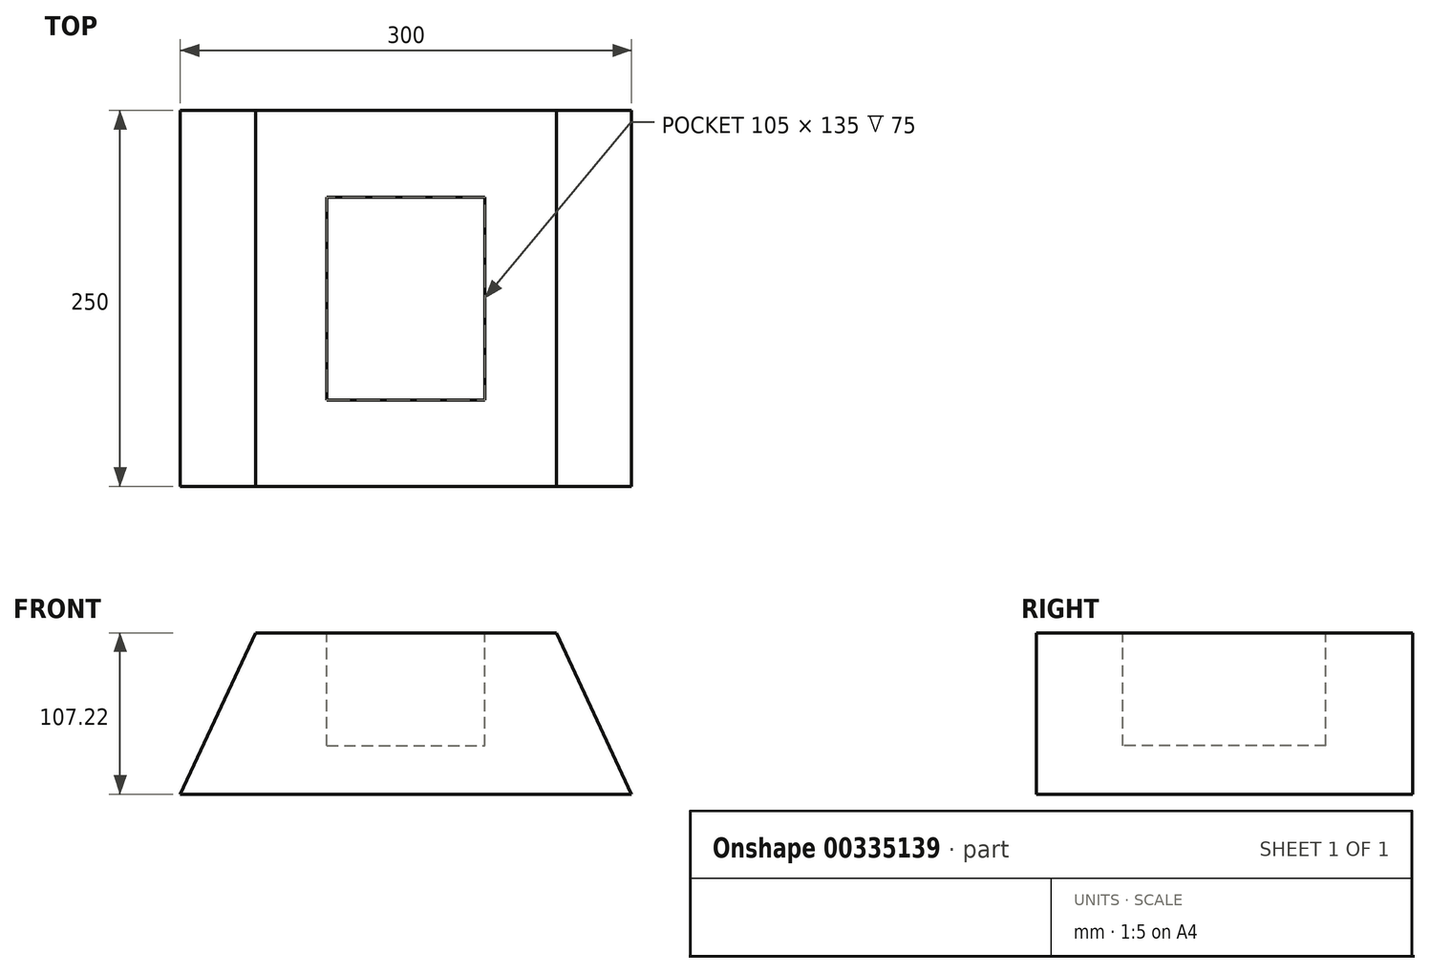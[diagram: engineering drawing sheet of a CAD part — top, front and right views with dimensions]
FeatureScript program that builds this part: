
annotation { "Feature Type Name" : "Feature", "Feature Type Description" : "" }
export const myFeature = defineFeature(function(context is Context, id is Id, definition is map)
    precondition{}
    {
        {
            var Q0;
            Q0=qCreatedBy(makeId("Front.planeOp"),FACE);
            var sketch = newSketch(context, id + "F0", { "sketchPlane" : qUnion([Q0])});
            skLineSegment(sketch, "E0.top", {"start": v(-124.12, -60.52) * mm, "end": v(175.88, -60.52) * mm});
            skLineSegment(sketch, "E1", {"start": v(-124.12, -60.52) * mm, "end": v(-74.12, 46.7) * mm});
            skLineSegment(sketch, "E2", {"start": v(-74.12, 46.7) * mm, "end": v(125.88, 46.7) * mm});
            skLineSegment(sketch, "E3", {"start": v(125.88, 46.7) * mm, "end": v(175.88, -60.52) * mm});
            skSolve(sketch);
        }
        {
            var Q0;
            Q0=makeQuery(id+"F0.imprint","IMPRINT",FACE,{"disambiguationData":[TD([[makeQuery(id+"F0.imprint","IMPRINT",EDGE,{"derivedFrom":sQuery(id+"F0.wireOp",EDGE,"E0.bottom")}),-1.0]])]});
            var Q1;
            Q1=makeQuery(id+"F0.imprint","IMPRINT",FACE,{"disambiguationData":[TD([[makeQuery(id+"F0.imprint","IMPRINT",EDGE,{"derivedFrom":sQuery(id+"F0.wireOp",EDGE,"E0.top")}),1.0]])]});
            extrude(context, id + "F1", {"entities" : qUnion([Q0, Q1]), "depth" : 250 * mm, "offsetDistance" : 25 * mm});
        }
        {
            var Q0;
            Q0=makeQuery(id+"F1.opExtrude","SWEPT_FACE",FACE,{"disambiguationData":[OSD([sQuery(id+"F0.wireOp",EDGE,"E2")])]});
            var sketch = newSketch(context, id + "F2", { "sketchPlane" : qUnion([Q0])});
            skLineSegment(sketch, "E4.bottom", {"start": v(-26.62, -57.5) * mm, "end": v(78.38, -57.5) * mm});
            skLineSegment(sketch, "E4.top", {"start": v(-26.62, -192.5) * mm, "end": v(78.38, -192.5) * mm});
            skLineSegment(sketch, "E4.left", {"start": v(-26.62, -57.5) * mm, "end": v(-26.62, -192.5) * mm});
            skLineSegment(sketch, "E4.right", {"start": v(78.38, -57.5) * mm, "end": v(78.38, -192.5) * mm});
            skSolve(sketch);
        }
        {
            var Q0;
            Q0=makeQuery(id+"F2.imprint","IMPRINT",FACE,{"disambiguationData":[TD([[makeQuery(id+"F2.imprint","IMPRINT",EDGE,{"derivedFrom":sQuery(id+"F2.wireOp",EDGE,"E4.bottom")}),-1.0]])]});
            extrude(context, id + "F3", {"entities" : qUnion([Q0]), "operationType" : NewBodyOperationType.REMOVE, "oppositeDirection" : true, "depth" : 75 * mm, "offsetDistance" : 25 * mm});
        }
    });
